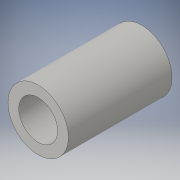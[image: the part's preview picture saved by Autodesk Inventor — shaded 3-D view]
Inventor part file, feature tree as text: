
AUTODESK INVENTOR PART (.ipt)
format: ipt  version: 2016 (Build 200138000, 138)  size: 92,160 bytes
history: native  units: in
note: dims shown in document units (in); Inventor stores cm internally (conversion verified against a paired STEP export)
features: extrude x1, sketch x1
ambient origin geometry x8: Origin, YZ Plane, XZ Plane, XY Plane, X Axis, Y Axis, Z Axis, Center Point
bodies: Solid1 (feature_tree)
feature tree (2):
  extrude  "Extrusion1"  Depth=0.4724in
  sketch  "Sketch1"  dims[d0=0.1772in d1=0.2756in d2=0.4724in d3=0.0in]
